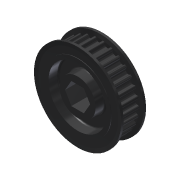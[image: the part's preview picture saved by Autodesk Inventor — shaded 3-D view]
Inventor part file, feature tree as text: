
AUTODESK INVENTOR PART (.ipt)
format: ipt  version: 2013 (Build 170138000, 138)  size: 969,728 bytes
history: native  units: in
note: dims shown in document units (in); Inventor stores cm internally (conversion verified against a paired STEP export)
features: mirror x1, other x1, imported_body x1
ambient origin geometry x8: Origin, YZ Plane, XZ Plane, XY Plane, X Axis, Y Axis, Z Axis, Center Point
feature tree (3):
  mirror  "Mirror1"
  other  "217-3229-STEP1"
  imported_body  "Base1"
